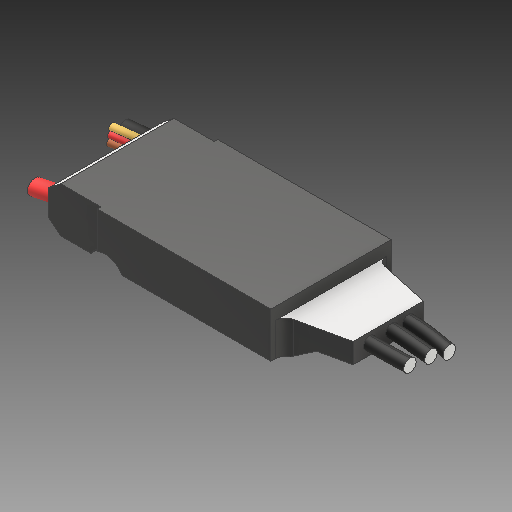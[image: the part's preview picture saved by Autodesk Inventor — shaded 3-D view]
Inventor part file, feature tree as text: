
AUTODESK INVENTOR PART (.ipt)
format: ipt  version: 2018 (Build 220112000, 112)  size: 985,088 bytes
history: native  units: mm
features: other x3, sketch x1
ambient origin geometry x8: Origin, YZ Plane, XZ Plane, XY Plane, X Axis, Y Axis, Z Axis, Center Point
bodies: Volumenkörper1 (feature_tree)
feature tree (4):
  other  "28-2-2013-001 - ESC Flyduino SimonK 20A body.ipt"
  other  "Volumenkörper1::28-2-2013-001 - ESC Flyduino SimonK 20A body.ipt"
  other  "Bezeichnung1"
  sketch  "Skizze1"  dims[d0=10.0mm]
